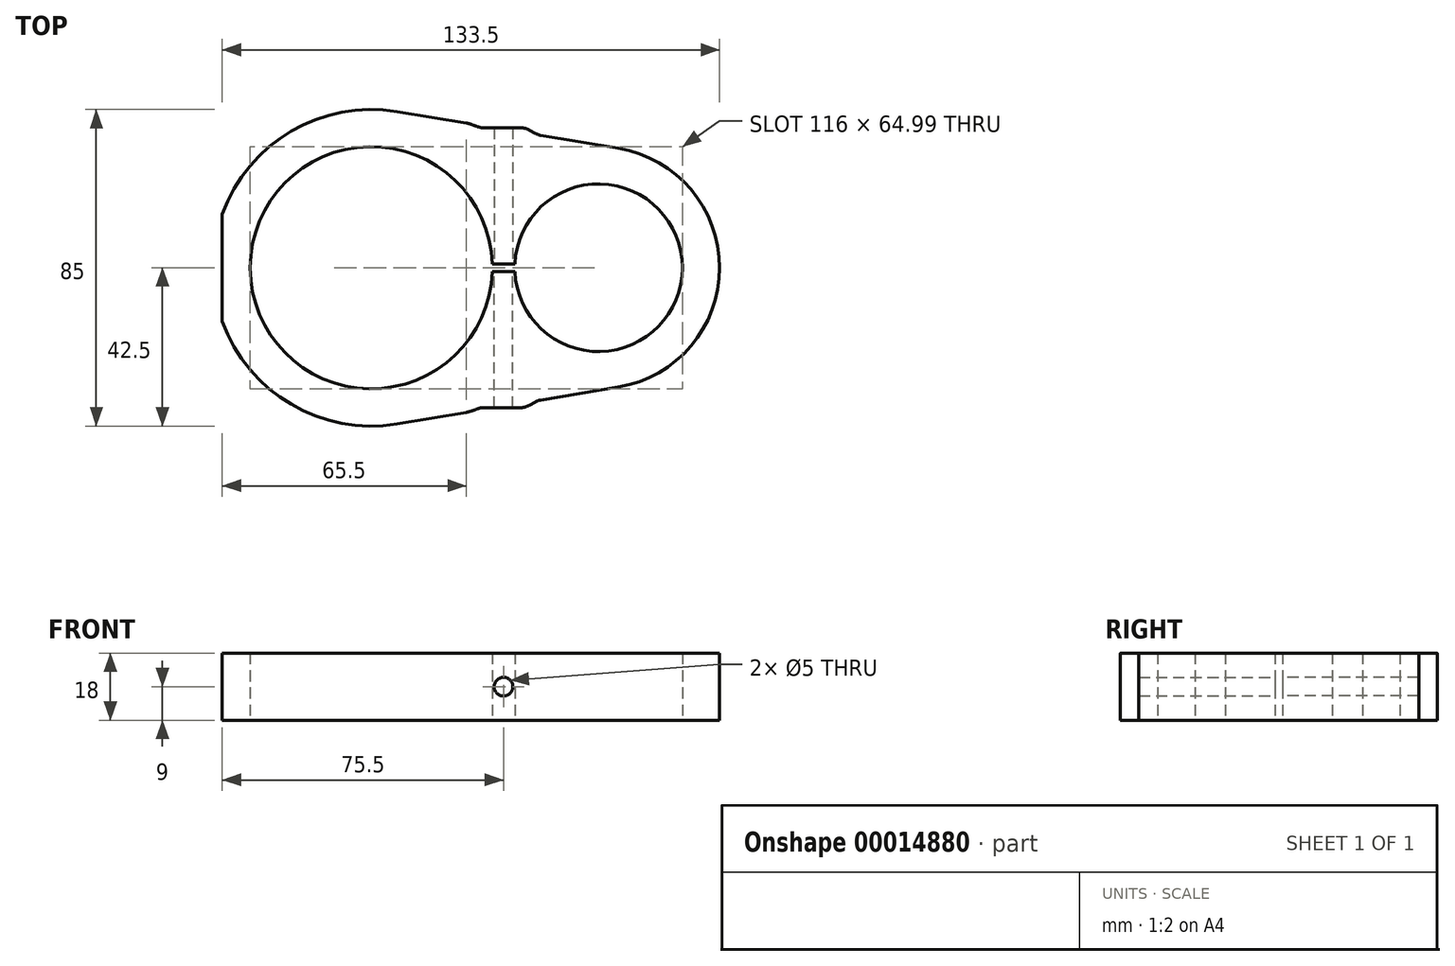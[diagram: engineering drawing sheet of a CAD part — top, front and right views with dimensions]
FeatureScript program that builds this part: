
annotation { "Feature Type Name" : "Feature", "Feature Type Description" : "" }
export const myFeature = defineFeature(function(context is Context, id is Id, definition is map)
    precondition{}
    {
        {
            var Q0;
            Q0=qCreatedBy(makeId("Top.planeOp"),FACE);
            var sketch = newSketch(context, id + "F0", { "sketchPlane" : qUnion([Q0])});
            skArc(sketch, "E0", {"start": v(66.33, -32.06) * mm, "mid": v(85.8, -21.01) * mm, "end": v(93.5, 0) * mm});
            skLineSegment(sketch, "E1", {"start": v(6.97, -41.93) * mm, "end": v(25.5, -38.84) * mm});
            skArc(sketch, "E2", {"start": v(-32.5, 0) * mm, "mid": v(-0.5, -32.5) * mm, "end": v(32.48, -1) * mm});
            skArc(sketch, "E3", {"start": v(38.52, -1) * mm, "mid": v(61.5, -22.5) * mm, "end": v(83.5, 0) * mm});
            skPoint(sketch, "E4", {"position": v(32.5, 0) * mm});
            skLineSegment(sketch, "E5", {"start": v(30.5, 0) * mm, "end": v(32.5, 0) * mm, "construction": true});
            skPoint(sketch, "E6", {"position": v(38.5, 0) * mm});
            skLineSegment(sketch, "E7", {"start": v(-40, 0) * mm, "end": v(-40, -14.36) * mm});
            skArc(sketch, "E8.trimOffspring", {"start": v(-40, -14.36) * mm, "mid": v(-21.51, -36.65) * mm, "end": v(6.97, -41.93) * mm});
            skPoint(sketch, "E9", {"position": v(83.5, 0) * mm});
            skPoint(sketch, "E10", {"position": v(61, -22.5) * mm});
            skLineSegment(sketch, "E11", {"start": v(32.5, 0) * mm, "end": v(30.5, 0) * mm, "construction": true});
            skLineSegment(sketch, "E12", {"start": v(-32.5, 0) * mm, "end": v(-40, 0) * mm});
            skLineSegment(sketch, "E13", {"start": v(83.5, 0) * mm, "end": v(93.5, 0) * mm});
            skLineSegment(sketch, "E14", {"start": v(32.48, -1) * mm, "end": v(38.52, -1) * mm});
            skLineSegment(sketch, "E15", {"start": v(30.5, 0) * mm, "end": v(30.5, -37.55) * mm, "construction": true});
            skLineSegment(sketch, "E16", {"start": v(40.5, 0) * mm, "end": v(40.5, -36.35) * mm, "construction": true});
            skLineSegment(sketch, "E17", {"start": v(30.5, -37.55) * mm, "end": v(40.5, -37.55) * mm});
            skFitSpline(sketch, "E18", {"points": [v(40.5, -37.55) * mm, v(45.5, -35.52) * mm], "startDerivative": vector(4.9, 0) * mm, "endDerivative": vector(4.84, 0.8) * mm});
            skFitSpline(sketch, "E19", {"points": [v(30.5, -37.55) * mm, v(25.5, -38.84) * mm], "startDerivative": vector(-6.32, 0) * mm, "endDerivative": vector(-6.23, -1.04) * mm});
            skLineSegment(sketch, "E20.trimOffspring", {"start": v(45.5, -35.52) * mm, "end": v(66.33, -32.06) * mm});
            skPoint(sketch, "E21", {"position": v(35.5, -1) * mm});
            skLineSegment(sketch, "E22", {"start": v(35.5, -1) * mm, "end": v(35.5, -59.7) * mm, "construction": true});
            skLineSegment(sketch, "E23", {"start": v(25.5, -38.84) * mm, "end": v(25.5, -49.82) * mm, "construction": true});
            skLineSegment(sketch, "E24", {"start": v(45.5, -35.52) * mm, "end": v(45.5, -48.05) * mm, "construction": true});
            skLineSegment(sketch, "E25.trimOffspring", {"start": v(40.5, 0) * mm, "end": v(38.5, 0) * mm, "construction": true});
            skSolve(sketch);
        }
        {
            var Q0;
            {var subQ0=sQuery(id+"F0.wireOp",EDGE,"60779b0d-b204-4cb7-bf57-cdf23e3e8706");var subQ1=sQuery(id+"F0.wireOp",EDGE,"E0");var subQ8=makeQuery(id+"F0.imprint","INTERSECT",VERTEX,{"disambiguationData":[OD(0.0)],"derivedFrom":[subQ1,subQ0]});Q0=makeQuery(id+"F0.imprint","IMPRINT",FACE,{"disambiguationData":[TD([[makeQuery(id+"F0.imprint","IMPRINT",EDGE,{"disambiguationData":[TD([[subQ8,-1.0]])],"derivedFrom":subQ1}),-1.0]])]});}
            var Q1;
            {var subQ4=sQuery(id+"F0.wireOp",EDGE,"E0");var subQ7=makeQuery(id+"F0.imprint","INTERSECT",VERTEX,{"derivedFrom":[subQ4,sQuery(id+"F0.wireOp",EDGE,"fa2cf6cf-a3a4-4233-b63a-180b4a1ea1cf")]});Q1=makeQuery(id+"F0.imprint","IMPRINT",FACE,{"disambiguationData":[TD([[makeQuery(id+"F0.imprint","IMPRINT",EDGE,{"disambiguationData":[TD([[subQ7,-1.0]])],"derivedFrom":subQ4}),1.0]])]});}
            var Q2;
            {var subQ5=sQuery(id+"F0.wireOp",EDGE,"60779b0d-b204-4cb7-bf57-cdf23e3e8706");var subQ7=sQuery(id+"F0.wireOp",EDGE,"E0");var subQ9=makeQuery(id+"F0.imprint","INTERSECT",VERTEX,{"disambiguationData":[OD(0.0)],"derivedFrom":[subQ7,subQ5]});Q2=makeQuery(id+"F0.imprint","IMPRINT",FACE,{"disambiguationData":[TD([[makeQuery(id+"F0.imprint","IMPRINT",EDGE,{"disambiguationData":[TD([[subQ9,-1.0]])],"derivedFrom":subQ7}),1.0]])]});}
            var Q3;
            {var subQ3=sQuery(id+"F0.wireOp",EDGE,"E2");var subQ7=sQuery(id+"F0.wireOp",EDGE,"E0");var subQ8=makeQuery(id+"F0.imprint","INTERSECT",VERTEX,{"disambiguationData":[OD(1.0)],"derivedFrom":[subQ7,subQ3]});Q3=makeQuery(id+"F0.imprint","IMPRINT",FACE,{"disambiguationData":[TD([[makeQuery(id+"F0.imprint","IMPRINT",EDGE,{"disambiguationData":[TD([[subQ8,-1.0]])],"derivedFrom":subQ7}),1.0]])]});}
            var Q4;
            {var subQ0=sQuery(id+"F0.wireOp",EDGE,"E1");Q4=makeQuery(id+"F0.imprint","IMPRINT",FACE,{"disambiguationData":[TD([[makeQuery(id+"F0.imprint","IMPRINT",EDGE,{"derivedFrom":subQ0}),1.0]])]});}
            var Q5;
            {var subQ0=sQuery(id+"F0.wireOp",EDGE,"fa2cf6cf-a3a4-4233-b63a-180b4a1ea1cf");Q5=makeQuery(id+"F0.imprint","IMPRINT",FACE,{"disambiguationData":[TD([[makeQuery(id+"F0.imprint","IMPRINT",EDGE,{"derivedFrom":subQ0}),-1.0]])]});}
            var Q6;
            {var subQ1=sQuery(id+"F0.wireOp",EDGE,"390d4679-ff10-4c7d-84da-3d8db24925aa");Q6=makeQuery(id+"F0.imprint","IMPRINT",FACE,{"disambiguationData":[TD([[makeQuery(id+"F0.imprint","IMPRINT",EDGE,{"derivedFrom":subQ1}),1.0]])]});}
            extrude(context, id + "F1", {"entities" : qUnion([Q0, Q1, Q2, Q3, Q4, Q5, Q6]), "depth" : 18 * mm});
        }
        {
            var Q0;
            Q0=qCreatedBy(makeId("Front.planeOp"),FACE);
            var sketch = newSketch(context, id + "F2", { "sketchPlane" : qUnion([Q0])});
            skLineSegment(sketch, "E26", {"start": v(32.5, 18) * mm, "end": v(38.5, 18) * mm});
            skPoint(sketch, "E27", {"position": v(35.5, 18) * mm});
            skLineSegment(sketch, "E28", {"start": v(35.5, 18) * mm, "end": v(35.5, 0) * mm});
            skPoint(sketch, "E29", {"position": v(35.5, 9) * mm});
            skSolve(sketch);
        }
        {
            var Q0;
            Q0=sQuery(id+"F2.wireOp",VERTEX,"E29");
            var Q1;
            Q1=makeQuery(id+"F1.opExtrude","SWEPT_BODY",BODY,{"disambiguationData":[OSD([sQuery(id+"F0.wireOp",EDGE,"E0"),sQuery(id+"F0.wireOp",EDGE,"E1"),sQuery(id+"F0.wireOp",EDGE,"fa2cf6cf-a3a4-4233-b63a-180b4a1ea1cf"),sQuery(id+"F0.wireOp",EDGE,"E2"),sQuery(id+"F0.wireOp",EDGE,"E3"),sQuery(id+"F0.wireOp",EDGE,"E7"),sQuery(id+"F0.wireOp",EDGE,"318f4db6-fbb2-4f2c-85ed-01272f5a5619.trimOffspring"),sQuery(id+"F0.wireOp",EDGE,"E8.trimOffspring")])]});
            hole(context, id + "F3", {"style" : HoleStyle.SIMPLE, "holeDiameter" : 5 * mm, "endStyle" : HoleEndStyle.THROUGH, "oppositeDirection" : true, "locations" : qUnion([Q0]), "scope" : qUnion([Q1])});
        }
        {
            var Q0;
            Q0=makeQuery(id+"F1.opExtrude","SWEPT_BODY",BODY,{"disambiguationData":[OSD([sQuery(id+"F0.wireOp",EDGE,"E0"),sQuery(id+"F0.wireOp",EDGE,"E1"),sQuery(id+"F0.wireOp",EDGE,"E2"),sQuery(id+"F0.wireOp",EDGE,"E3"),sQuery(id+"F0.wireOp",EDGE,"E5"),sQuery(id+"F0.wireOp",EDGE,"E7"),sQuery(id+"F0.wireOp",EDGE,"E8.trimOffspring"),sQuery(id+"F0.wireOp",EDGE,"E12"),sQuery(id+"F0.wireOp",EDGE,"E13")])]});
            var Q1;
            Q1=qCreatedBy(makeId("Front.planeOp"),FACE);
            mirror(context, id + "F4", {"operationType" : NewBodyOperationType.ADD, "entities" : qUnion([Q0]), "mirrorPlane" : qUnion([Q1])});
        }
    });
